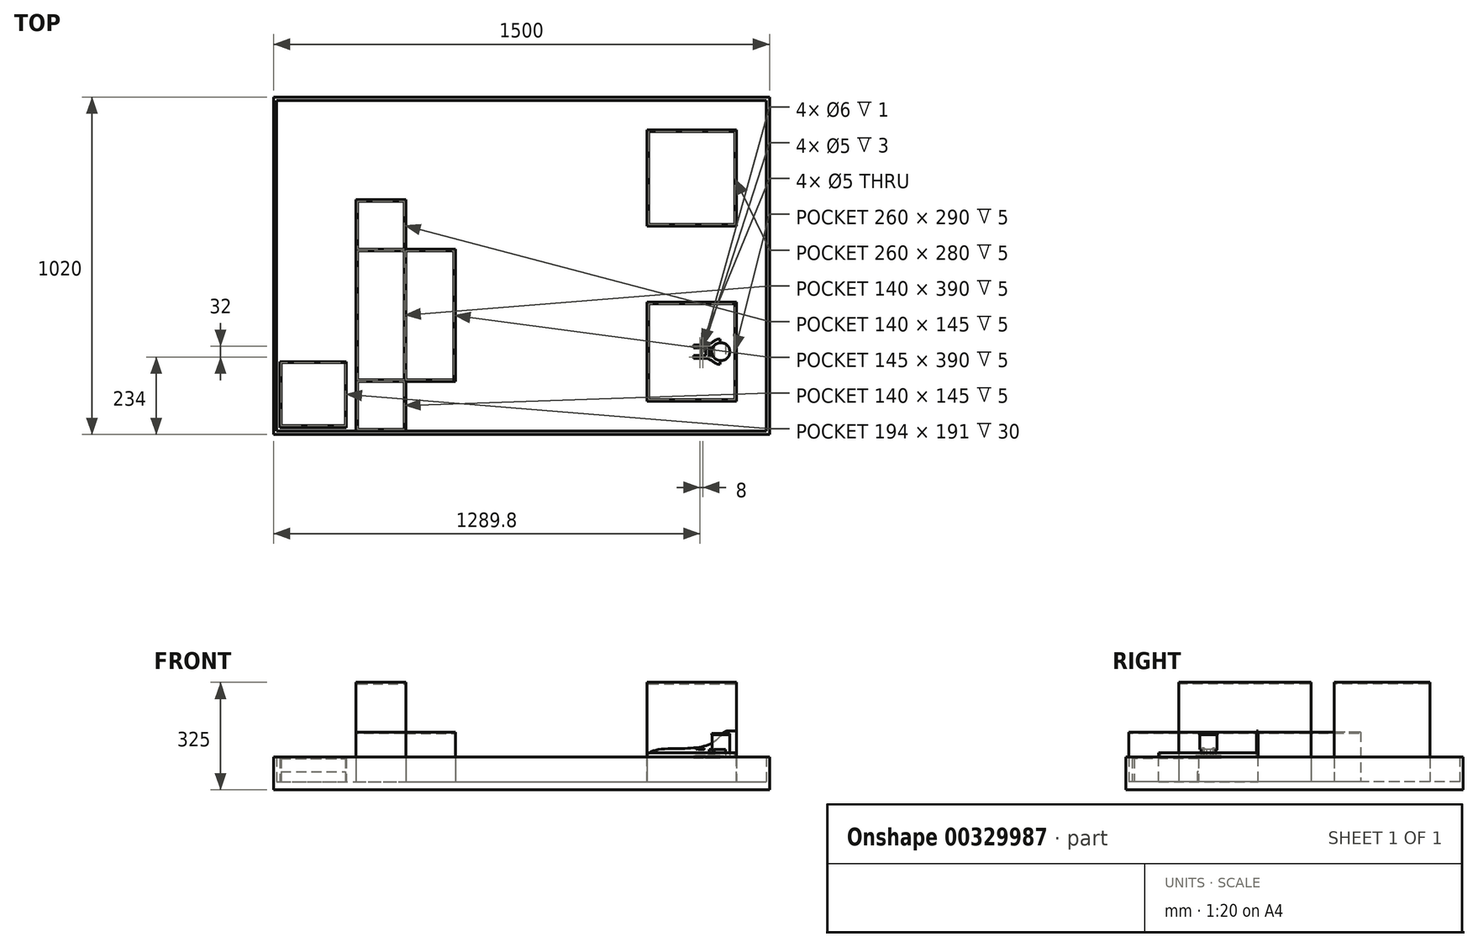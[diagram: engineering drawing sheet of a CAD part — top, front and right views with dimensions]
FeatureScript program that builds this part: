
annotation { "Feature Type Name" : "Feature", "Feature Type Description" : "" }
export const myFeature = defineFeature(function(context is Context, id is Id, definition is map)
    precondition{}
    {
        {
            var Q0;
            Q0=qCreatedBy(makeId("Top.planeOp"),FACE);
            var sketch = newSketch(context, id + "F0", { "sketchPlane" : qUnion([Q0])});
            skCircle(sketch, "E0", {"center": v(0, 0) * mm, "radius": 27.2 * mm});
            skSolve(sketch);
        }
        {
            var Q0;
            Q0=qSketchRegion(id+"F0",true);
            extrude(context, id + "F1", {"entities" : qUnion([Q0]), "depth" : 2.83 * mm});
        }
        {
            var Q0;
            Q0=makeQuery(id+"F1.opExtrude","CAP_FACE",FACE,{"disambiguationData":[OSD([sQuery(id+"F0.wireOp",EDGE,"E0")])],"isStart":false});
            var sketch = newSketch(context, id + "F2", { "sketchPlane" : qUnion([Q0])});
            skCircle(sketch, "E1", {"center": v(0, 0) * mm, "radius": 26.4 * mm});
            skSolve(sketch);
        }
        {
            var Q0;
            Q0=qSketchRegion(id+"F2",true);
            extrude(context, id + "F3", {"entities" : qUnion([Q0]), "operationType" : NewBodyOperationType.ADD, "depth" : 67.36 * mm});
        }
        {
            var Q0;
            Q0=makeQuery(id+"F3.opExtrude","CAP_FACE",FACE,{"disambiguationData":[OSD([sQuery(id+"F2.wireOp",EDGE,"E1")])],"isStart":false});
            var sketch = newSketch(context, id + "F4", { "sketchPlane" : qUnion([Q0])});
            skCircle(sketch, "E2", {"center": v(0, 0) * mm, "radius": 27.2 * mm});
            skSolve(sketch);
        }
        {
            var Q0;
            Q0=qSketchRegion(id+"F4",true);
            extrude(context, id + "F5", {"entities" : qUnion([Q0]), "operationType" : NewBodyOperationType.ADD, "depth" : 2.83 * mm});
        }
        {
            var Q0;
            Q0=makeQuery(id+"F5.opExtrude","CAP_FACE",FACE,{"disambiguationData":[OSD([sQuery(id+"F4.wireOp",EDGE,"E2")])],"isStart":false});
            var sketch = newSketch(context, id + "F6", { "sketchPlane" : qUnion([Q0])});
            skSolve(sketch);
        }
        {
            var Q0;
            Q0=qCreatedBy(makeId("Top.planeOp"),FACE);
            cPlane(context, id + "F7", {"entities" : qUnion([Q0]), "cplaneType" : CPlaneType.OFFSET, "offset" : 25 * mm, "width" : 150 * mm, "height" : 150 * mm});
        }
        {
            var Q0;
            Q0=makeQuery(id+"F6.imprint","IMPRINT",FACE,{"disambiguationData":[TD([[makeQuery(id+"F6.imprint","IMPRINT",EDGE,{"derivedFrom":makeQuery(id+"F5.opExtrude","CAP_EDGE",EDGE,{"disambiguationData":[OSD([sQuery(id+"F4.wireOp",EDGE,"E2")])],"isStart":false})}),1.0]])]});
            var sketch = newSketch(context, id + "F8", { "sketchPlane" : qUnion([Q0])});
            skSolve(sketch);
        }
        {
            var Q0;
            Q0=qCreatedBy(makeId("Top.planeOp"),FACE);
            var sketch = newSketch(context, id + "F9", { "sketchPlane" : qUnion([Q0])});
            skLineSegment(sketch, "E3.bottom", {"start": v(-222.8, -150) * mm, "end": v(47.2, -150) * mm});
            skLineSegment(sketch, "E3.top", {"start": v(-222.8, 150) * mm, "end": v(47.2, 150) * mm});
            skLineSegment(sketch, "E3.left", {"start": v(-222.8, -150) * mm, "end": v(-222.8, 150) * mm});
            skLineSegment(sketch, "E3.right", {"start": v(47.2, -150) * mm, "end": v(47.2, 150) * mm});
            skSolve(sketch);
        }
        {
            var Q0;
            Q0=qSketchRegion(id+"F9",true);
            extrude(context, id + "F10", {"entities" : qUnion([Q0]), "oppositeDirection" : true, "depth" : 72 * mm});
        }
        {
            var Q0;
            Q0=makeQuery(id+"F10.opExtrude","CAP_FACE",FACE,{"disambiguationData":[OSD([sQuery(id+"F9.wireOp",EDGE,"E3.bottom"),sQuery(id+"F9.wireOp",EDGE,"E3.top"),sQuery(id+"F9.wireOp",EDGE,"E3.left"),sQuery(id+"F9.wireOp",EDGE,"E3.right")])],"isStart":true});
            var sketch = newSketch(context, id + "F11", { "sketchPlane" : qUnion([Q0])});
            skLineSegment(sketch, "E4.bottom", {"start": v(-222.8, -150) * mm, "end": v(47.2, -150) * mm});
            skLineSegment(sketch, "E4.top", {"start": v(-222.8, -145) * mm, "end": v(42.2, -145) * mm});
            skLineSegment(sketch, "E4.left", {"start": v(-222.8, -150) * mm, "end": v(-222.8, -145) * mm});
            skLineSegment(sketch, "E5.bottom", {"start": v(47.2, 150) * mm, "end": v(42.2, 150) * mm});
            skLineSegment(sketch, "E5.left", {"start": v(47.2, 150) * mm, "end": v(47.2, -150) * mm});
            skLineSegment(sketch, "E5.right", {"start": v(42.2, 150) * mm, "end": v(42.2, -145) * mm});
            skSolve(sketch);
        }
        {
            var Q0;
            Q0=qSketchRegion(id+"F11",true);
            extrude(context, id + "F12", {"entities" : qUnion([Q0]), "operationType" : NewBodyOperationType.ADD, "depth" : 15 * mm});
        }
        {
            var Q0;
            Q0=makeQuery(id+"F12.boolean.opBoolean","MERGE",FACE,{"derivedFrom":[makeQuery(id+"F10.opExtrude","SWEPT_FACE",FACE,{"disambiguationData":[OSD([sQuery(id+"F9.wireOp",EDGE,"E3.top")])]}),makeQuery(id+"F12.opExtrude","SWEPT_FACE",FACE,{"disambiguationData":[OSD([sQuery(id+"F11.wireOp",EDGE,"E5.bottom")])]})]});
            var sketch = newSketch(context, id + "F13", { "sketchPlane" : qUnion([Q0])});
            skLineSegment(sketch, "E6", {"start": v(-47.2, 81.36) * mm, "end": v(-21.31, 81.36) * mm});
            skFitSpline(sketch, "E7", {"points": [v(-21.31, 81.36) * mm, v(15.24, 52.01) * mm, v(114.14, 28.17) * mm, v(222.8, 0) * mm], "startDerivative": vector(181.02, 0.3) * mm, "endDerivative": vector(-1.73, -239.85) * mm});
            skLineSegment(sketch, "E8", {"start": v(-47.2, 81.36) * mm, "end": v(-47.2, -72) * mm});
            skLineSegment(sketch, "E9", {"start": v(-47.2, -72) * mm, "end": v(222.8, -72) * mm});
            skLineSegment(sketch, "E10", {"start": v(222.8, -72) * mm, "end": v(222.8, 0) * mm});
            skSolve(sketch);
        }
        {
            var Q0;
            Q0=qSketchRegion(id+"F13",true);
            extrude(context, id + "F14", {"entities" : qUnion([Q0]), "operationType" : NewBodyOperationType.ADD, "oppositeDirection" : true, "depth" : 5 * mm});
        }
        {
            var Q0;
            Q0=makeQuery(id+"F10.opExtrude","CAP_FACE",FACE,{"disambiguationData":[OSD([sQuery(id+"F9.wireOp",EDGE,"E3.bottom"),sQuery(id+"F9.wireOp",EDGE,"E3.top"),sQuery(id+"F9.wireOp",EDGE,"E3.left"),sQuery(id+"F9.wireOp",EDGE,"E3.right")])],"isStart":true});
            var sketch = newSketch(context, id + "F15", { "sketchPlane" : qUnion([Q0])});
            skLineSegment(sketch, "E11.bottom", {"start": v(-222.8, 145) * mm, "end": v(-217.8, 145) * mm});
            skLineSegment(sketch, "E11.top", {"start": v(-222.8, -145) * mm, "end": v(-217.8, -145) * mm});
            skLineSegment(sketch, "E11.left", {"start": v(-222.8, 145) * mm, "end": v(-222.8, -145) * mm});
            skLineSegment(sketch, "E11.right", {"start": v(-217.8, 145) * mm, "end": v(-217.8, -145) * mm});
            skSolve(sketch);
        }
        {
            var Q0;
            Q0=qSketchRegion(id+"F15",true);
            extrude(context, id + "F16", {"entities" : qUnion([Q0]), "operationType" : NewBodyOperationType.ADD, "depth" : 5 * mm});
        }
        {
            var Q0;
            Q0=makeQuery(id+"F10.opExtrude","CAP_FACE",FACE,{"disambiguationData":[OSD([sQuery(id+"F9.wireOp",EDGE,"E3.bottom"),sQuery(id+"F9.wireOp",EDGE,"E3.top"),sQuery(id+"F9.wireOp",EDGE,"E3.left"),sQuery(id+"F9.wireOp",EDGE,"E3.right")])],"isStart":false});
            var sketch = newSketch(context, id + "F17", { "sketchPlane" : qUnion([Q0])});
            skLineSegment(sketch, "E12.bottom", {"start": v(147.2, 250) * mm, "end": v(-1352.8, 250) * mm});
            skLineSegment(sketch, "E12.top", {"start": v(147.2, -770) * mm, "end": v(-1352.8, -770) * mm});
            skLineSegment(sketch, "E12.left", {"start": v(147.2, 250) * mm, "end": v(147.2, -770) * mm});
            skLineSegment(sketch, "E12.right", {"start": v(-1352.8, 250) * mm, "end": v(-1352.8, -770) * mm});
            skSolve(sketch);
        }
        {
            var Q0;
            Q0=qSketchRegion(id+"F17",true);
            extrude(context, id + "F18", {"entities" : qUnion([Q0]), "operationType" : NewBodyOperationType.ADD, "depth" : 25 * mm});
        }
        {
            var Q0;
            Q0=makeQuery(id+"F18.opExtrude","CAP_FACE",FACE,{"disambiguationData":[OSD([sQuery(id+"F17.wireOp",EDGE,"E12.bottom"),sQuery(id+"F17.wireOp",EDGE,"E12.top"),sQuery(id+"F17.wireOp",EDGE,"E12.left"),sQuery(id+"F17.wireOp",EDGE,"E12.right")])],"isStart":true});
            var sketch = newSketch(context, id + "F19", { "sketchPlane" : qUnion([Q0])});
            skLineSegment(sketch, "E13.bottom", {"start": v(-222.8, 670) * mm, "end": v(47.2, 670) * mm});
            skLineSegment(sketch, "E13.top", {"start": v(-222.8, 380) * mm, "end": v(47.2, 380) * mm});
            skLineSegment(sketch, "E13.left", {"start": v(-222.8, 670) * mm, "end": v(-222.8, 380) * mm});
            skLineSegment(sketch, "E13.right", {"start": v(47.2, 670) * mm, "end": v(47.2, 380) * mm});
            skSolve(sketch);
        }
        {
            var Q0;
            Q0=qSketchRegion(id+"F19",true);
            extrude(context, id + "F20", {"entities" : qUnion([Q0]), "operationType" : NewBodyOperationType.ADD, "depth" : 300 * mm});
        }
        {
            var Q0;
            Q0=makeQuery(id+"F20.opExtrude","CAP_FACE",FACE,{"disambiguationData":[OSD([sQuery(id+"F19.wireOp",EDGE,"E13.bottom"),sQuery(id+"F19.wireOp",EDGE,"E13.top"),sQuery(id+"F19.wireOp",EDGE,"E13.left"),sQuery(id+"F19.wireOp",EDGE,"E13.right")])],"isStart":false});
            var sketch = newSketch(context, id + "F21", { "sketchPlane" : qUnion([Q0])});
            skLineSegment(sketch, "E14.bottom", {"start": v(-217.8, 665) * mm, "end": v(42.2, 665) * mm});
            skLineSegment(sketch, "E14.top", {"start": v(-217.8, 385) * mm, "end": v(42.2, 385) * mm});
            skLineSegment(sketch, "E14.left", {"start": v(-217.8, 665) * mm, "end": v(-217.8, 385) * mm});
            skLineSegment(sketch, "E14.right", {"start": v(42.2, 665) * mm, "end": v(42.2, 385) * mm});
            skSolve(sketch);
        }
        {
            var Q0;
            Q0=qSketchRegion(id+"F21",true);
            extrude(context, id + "F22", {"entities" : qUnion([Q0]), "operationType" : NewBodyOperationType.REMOVE, "oppositeDirection" : true, "depth" : 5 * mm});
        }
        {
            var Q0;
            Q0=makeQuery(id+"F18.opExtrude","CAP_FACE",FACE,{"disambiguationData":[OSD([sQuery(id+"F17.wireOp",EDGE,"E12.bottom"),sQuery(id+"F17.wireOp",EDGE,"E12.top"),sQuery(id+"F17.wireOp",EDGE,"E12.left"),sQuery(id+"F17.wireOp",EDGE,"E12.right")])],"isStart":true});
            var sketch = newSketch(context, id + "F23", { "sketchPlane" : qUnion([Q0])});
            skLineSegment(sketch, "E15.bottom", {"start": v(-1352.8, 770) * mm, "end": v(147.2, 770) * mm});
            skLineSegment(sketch, "E15.top", {"start": v(-1352.8, -250) * mm, "end": v(147.2, -250) * mm});
            skLineSegment(sketch, "E15.left", {"start": v(-1352.8, 770) * mm, "end": v(-1352.8, -250) * mm});
            skLineSegment(sketch, "E15.right", {"start": v(147.2, 770) * mm, "end": v(147.2, -250) * mm});
            skLineSegment(sketch, "E16.bottom", {"start": v(-1342.8, 760) * mm, "end": v(137.2, 760) * mm});
            skLineSegment(sketch, "E16.top", {"start": v(-1342.8, -240) * mm, "end": v(137.2, -240) * mm});
            skLineSegment(sketch, "E16.left", {"start": v(-1342.8, 760) * mm, "end": v(-1342.8, -240) * mm});
            skLineSegment(sketch, "E16.right", {"start": v(137.2, 760) * mm, "end": v(137.2, -240) * mm});
            skSolve(sketch);
        }
        {
            var Q0;
            Q0=qSketchRegion(id+"F23",true);
            extrude(context, id + "F24", {"entities" : qUnion([Q0]), "operationType" : NewBodyOperationType.ADD, "depth" : 75 * mm});
        }
        {
            var Q0;
            Q0=makeQuery(id+"F18.opExtrude","CAP_FACE",FACE,{"disambiguationData":[OSD([sQuery(id+"F17.wireOp",EDGE,"E12.bottom"),sQuery(id+"F17.wireOp",EDGE,"E12.top"),sQuery(id+"F17.wireOp",EDGE,"E12.left"),sQuery(id+"F17.wireOp",EDGE,"E12.right")])],"isStart":true});
            var sketch = newSketch(context, id + "F25", { "sketchPlane" : qUnion([Q0])});
            skLineSegment(sketch, "E17.bottom", {"start": v(-1102.8, 460) * mm, "end": v(-952.8, 460) * mm});
            skLineSegment(sketch, "E17.top", {"start": v(-1102.8, -240) * mm, "end": v(-952.8, -240) * mm});
            skLineSegment(sketch, "E17.left", {"start": v(-1102.8, 460) * mm, "end": v(-1102.8, -240) * mm});
            skLineSegment(sketch, "E17.right", {"start": v(-952.8, 460) * mm, "end": v(-952.8, 310) * mm});
            skLineSegment(sketch, "E18.bottom", {"start": v(-952.8, 310) * mm, "end": v(-802.8, 310) * mm});
            skLineSegment(sketch, "E18.top", {"start": v(-952.8, -90) * mm, "end": v(-802.8, -90) * mm});
            skLineSegment(sketch, "E18.right", {"start": v(-802.8, 310) * mm, "end": v(-802.8, -90) * mm});
            skLineSegment(sketch, "E19.trimOffspring", {"start": v(-952.8, -90) * mm, "end": v(-952.8, -240) * mm});
            skSolve(sketch);
        }
        {
            var Q0;
            Q0=qSketchRegion(id+"F25",true);
            extrude(context, id + "F26", {"entities" : qUnion([Q0]), "operationType" : NewBodyOperationType.ADD, "depth" : 150 * mm});
        }
        {
            var Q0;
            Q0=makeQuery(id+"F26.opExtrude","CAP_FACE",FACE,{"disambiguationData":[OSD([sQuery(id+"F25.wireOp",EDGE,"E17.bottom"),sQuery(id+"F25.wireOp",EDGE,"E17.top"),sQuery(id+"F25.wireOp",EDGE,"E17.left"),sQuery(id+"F25.wireOp",EDGE,"E17.right"),sQuery(id+"F25.wireOp",EDGE,"E18.bottom"),sQuery(id+"F25.wireOp",EDGE,"E18.top"),sQuery(id+"F25.wireOp",EDGE,"E18.right"),sQuery(id+"F25.wireOp",EDGE,"E19.trimOffspring")])],"isStart":false});
            var sketch = newSketch(context, id + "F27", { "sketchPlane" : qUnion([Q0])});
            skLineSegment(sketch, "E20.bottom", {"start": v(-952.8, 310) * mm, "end": v(-1102.8, 310) * mm});
            skLineSegment(sketch, "E20.top", {"start": v(-952.8, -90) * mm, "end": v(-1102.8, -90) * mm});
            skLineSegment(sketch, "E20.left", {"start": v(-952.8, 310) * mm, "end": v(-952.8, -90) * mm});
            skLineSegment(sketch, "E20.right", {"start": v(-1102.8, 310) * mm, "end": v(-1102.8, -90) * mm});
            skSolve(sketch);
        }
        {
            var Q0;
            Q0=qSketchRegion(id+"F27",true);
            extrude(context, id + "F28", {"entities" : qUnion([Q0]), "operationType" : NewBodyOperationType.ADD, "depth" : 150 * mm});
        }
        {
            var Q0;
            Q0=makeQuery(id+"F28.opExtrude","CAP_FACE",FACE,{"disambiguationData":[OSD([sQuery(id+"F27.wireOp",EDGE,"E20.bottom"),sQuery(id+"F27.wireOp",EDGE,"E20.top"),sQuery(id+"F27.wireOp",EDGE,"E20.left"),sQuery(id+"F27.wireOp",EDGE,"E20.right")])],"isStart":false});
            var sketch = newSketch(context, id + "F29", { "sketchPlane" : qUnion([Q0])});
            skLineSegment(sketch, "E21.bottom", {"start": v(-1097.8, 305) * mm, "end": v(-957.8, 305) * mm});
            skLineSegment(sketch, "E21.top", {"start": v(-1097.8, -85) * mm, "end": v(-957.8, -85) * mm});
            skLineSegment(sketch, "E21.left", {"start": v(-1097.8, 305) * mm, "end": v(-1097.8, -85) * mm});
            skLineSegment(sketch, "E21.right", {"start": v(-957.8, 305) * mm, "end": v(-957.8, -85) * mm});
            skSolve(sketch);
        }
        {
            var Q0;
            Q0=qSketchRegion(id+"F29",true);
            extrude(context, id + "F30", {"entities" : qUnion([Q0]), "operationType" : NewBodyOperationType.REMOVE, "oppositeDirection" : true, "depth" : 5 * mm});
        }
        {
            var Q0;
            {var subQ0=sQuery(id+"F25.wireOp",EDGE,"E17.left");var subQ1=sQuery(id+"F25.wireOp",EDGE,"E18.bottom");var subQ2=sQuery(id+"F25.wireOp",EDGE,"E17.right");var subQ3=sQuery(id+"F25.wireOp",EDGE,"E17.bottom");var subQ4=makeQuery(id+"F26.opExtrude","CAP_FACE",FACE,{"disambiguationData":[OSD([subQ3,sQuery(id+"F25.wireOp",EDGE,"E17.top"),subQ0,subQ2,subQ1,sQuery(id+"F25.wireOp",EDGE,"E18.top"),sQuery(id+"F25.wireOp",EDGE,"E18.right"),sQuery(id+"F25.wireOp",EDGE,"E19.trimOffspring")])],"isStart":false});Q0=makeQuery(id+"F28.boolean.opBoolean","SPLIT",FACE,{"disambiguationData":[TD([makeQuery(id+"F26.opExtrude","SWEPT_FACE",FACE,{"disambiguationData":[OSD([subQ3])]})])],"derivedFrom":subQ4});}
            var sketch = newSketch(context, id + "F31", { "sketchPlane" : qUnion([Q0])});
            skLineSegment(sketch, "E22.bottom", {"start": v(-1097.8, 455) * mm, "end": v(-957.8, 455) * mm});
            skLineSegment(sketch, "E22.top", {"start": v(-1097.8, 310) * mm, "end": v(-957.8, 310) * mm});
            skLineSegment(sketch, "E22.left", {"start": v(-1097.8, 455) * mm, "end": v(-1097.8, 310) * mm});
            skLineSegment(sketch, "E22.right", {"start": v(-957.8, 455) * mm, "end": v(-957.8, 310) * mm});
            skLineSegment(sketch, "E23.bottom", {"start": v(-952.8, 305) * mm, "end": v(-807.8, 305) * mm});
            skLineSegment(sketch, "E23.top", {"start": v(-952.8, -85) * mm, "end": v(-807.8, -85) * mm});
            skLineSegment(sketch, "E23.left", {"start": v(-952.8, 305) * mm, "end": v(-952.8, -85) * mm});
            skLineSegment(sketch, "E23.right", {"start": v(-807.8, 305) * mm, "end": v(-807.8, -85) * mm});
            skLineSegment(sketch, "E24.bottom", {"start": v(-1097.8, -90) * mm, "end": v(-957.8, -90) * mm});
            skLineSegment(sketch, "E24.top", {"start": v(-1097.8, -235) * mm, "end": v(-957.8, -235) * mm});
            skLineSegment(sketch, "E24.left", {"start": v(-1097.8, -90) * mm, "end": v(-1097.8, -235) * mm});
            skLineSegment(sketch, "E24.right", {"start": v(-957.8, -90) * mm, "end": v(-957.8, -235) * mm});
            skSolve(sketch);
        }
        {
            var Q0;
            Q0=qSketchRegion(id+"F31",true);
            extrude(context, id + "F32", {"entities" : qUnion([Q0]), "operationType" : NewBodyOperationType.REMOVE, "oppositeDirection" : true, "depth" : 5 * mm});
        }
        {
            var Q0;
            Q0=qCreatedBy(id+"F7.planeOp",FACE);
            var sketch = newSketch(context, id + "F33", { "sketchPlane" : qUnion([Q0])});
            skLineSegment(sketch, "E25", {"start": v(0, 0) * mm, "end": v(-90, 0) * mm, "construction": true});
            skLineSegment(sketch, "E26.bottom", {"start": v(-74.5, -12) * mm, "end": v(-55, -12) * mm});
            skLineSegment(sketch, "E26.top", {"start": v(-74.5, -20) * mm, "end": v(-55, -20) * mm});
            skLineSegment(sketch, "E26.left", {"start": v(-74.5, -12) * mm, "end": v(-74.5, -13) * mm});
            skPoint(sketch, "E27.visualSharp", {"position": v(-51, -12) * mm});
            skPoint(sketch, "E28.visualSharp", {"position": v(-51, -20) * mm});
            skCircle(sketch, "E29", {"center": v(-55, -16) * mm, "radius": 3 * mm});
            skLineSegment(sketch, "E30", {"start": v(-59, -3.98) * mm, "end": v(-59, -18.08) * mm, "construction": true});
            skCircle(sketch, "E31.MirrorC", {"center": v(-63, -16) * mm, "radius": 3 * mm});
            skLineSegment(sketch, "E32.bottom", {"start": v(-74.5, -13) * mm, "end": v(-65.65, -13) * mm});
            skLineSegment(sketch, "E32.top", {"start": v(-74.5, -19) * mm, "end": v(-65.65, -19) * mm});
            skArc(sketch, "E33", {"start": v(-65.65, -13) * mm, "mid": v(-67, -16) * mm, "end": v(-65.65, -19) * mm});
            skLineSegment(sketch, "E34.trimOffspring", {"start": v(-74.5, -19) * mm, "end": v(-74.5, -20) * mm});
            skArc(sketch, "E35.trimOffspring", {"start": v(-55, -20) * mm, "mid": v(-51, -16) * mm, "end": v(-55, -12) * mm});
            skLineSegment(sketch, "E36.MirrorCS", {"start": v(-74.5, 12) * mm, "end": v(-74.5, 13) * mm});
            skLineSegment(sketch, "E37.MirrorCS", {"start": v(-74.5, 19) * mm, "end": v(-74.5, 20) * mm});
            skPoint(sketch, "E38.MirrorP", {"position": v(-51, 12) * mm});
            skLineSegment(sketch, "E39.MirrorCS", {"start": v(-74.5, 12) * mm, "end": v(-55, 12) * mm});
            skPoint(sketch, "E40.MirrorP", {"position": v(-51, 20) * mm});
            skArc(sketch, "E41.MirrorCS", {"start": v(-65.65, 13) * mm, "mid": v(-67, 16) * mm, "end": v(-65.65, 19) * mm});
            skArc(sketch, "E42.MirrorCS", {"start": v(-55, 20) * mm, "mid": v(-51, 16) * mm, "end": v(-55, 12) * mm});
            skLineSegment(sketch, "E43.MirrorCS", {"start": v(-74.5, 20) * mm, "end": v(-55, 20) * mm});
            skCircle(sketch, "E44.MirrorC", {"center": v(-55, 16) * mm, "radius": 3 * mm});
            skCircle(sketch, "E45.MirrorC", {"center": v(-63, 16) * mm, "radius": 3 * mm});
            skLineSegment(sketch, "E46.MirrorCS", {"start": v(-74.5, 19) * mm, "end": v(-65.65, 19) * mm});
            skLineSegment(sketch, "E47.MirrorCS", {"start": v(-74.5, 13) * mm, "end": v(-65.65, 13) * mm});
            skSolve(sketch);
        }
        {
            var Q0;
            Q0=qSketchRegion(id+"F33",true);
            var Q1;
            Q1=qSketchRegion(id+"F36",true);
            extrude(context, id + "F34", {"entities" : qUnion([Q0, Q1]), "endBound" : BoundingType.SYMMETRIC, "depth" : 8 * mm});
        }
        {
            var Q0;
            Q0=makeQuery(id+"F34.opExtrude","CAP_EDGE",EDGE,{"disambiguationData":[OSD([sQuery(id+"F33.wireOp",EDGE,"E34.trimOffspring")])],"isStart":false});
            var Q1;
            Q1=makeQuery(id+"F34.opExtrude","CAP_EDGE",EDGE,{"disambiguationData":[OSD([sQuery(id+"F33.wireOp",EDGE,"E26.left")])],"isStart":false});
            var Q2;
            Q2=makeQuery(id+"F34.opExtrude","CAP_EDGE",EDGE,{"disambiguationData":[OSD([sQuery(id+"F33.wireOp",EDGE,"E34.trimOffspring")])],"isStart":true});
            var Q3;
            Q3=makeQuery(id+"F34.opExtrude","CAP_EDGE",EDGE,{"disambiguationData":[OSD([sQuery(id+"F33.wireOp",EDGE,"E26.left")])],"isStart":true});
            var Q4;
            Q4=makeQuery(id+"F34.opExtrude","CAP_EDGE",EDGE,{"disambiguationData":[OSD([sQuery(id+"F33.wireOp",EDGE,"E36.MirrorCS")])],"isStart":false});
            var Q5;
            Q5=makeQuery(id+"F34.opExtrude","CAP_EDGE",EDGE,{"disambiguationData":[OSD([sQuery(id+"F33.wireOp",EDGE,"E37.MirrorCS")])],"isStart":false});
            var Q6;
            Q6=makeQuery(id+"F34.opExtrude","CAP_EDGE",EDGE,{"disambiguationData":[OSD([sQuery(id+"F33.wireOp",EDGE,"E37.MirrorCS")])],"isStart":true});
            var Q7;
            Q7=makeQuery(id+"F34.opExtrude","CAP_EDGE",EDGE,{"disambiguationData":[OSD([sQuery(id+"F33.wireOp",EDGE,"E36.MirrorCS")])],"isStart":true});
            fillet(context, id + "F35", {"entities" : qUnion([Q0, Q1, Q2, Q3, Q4, Q5, Q6, Q7]), "radius" : 4 * mm, "tangentPropagation" : true, "allowEdgeOverflow" : false});
        }
        {
            var Q0;
            Q0=makeQuery(id+"F34.opExtrude","SWEPT_FACE",FACE,{"disambiguationData":[OSD([sQuery(id+"F33.wireOp",EDGE,"E26.top")])]});
            var sketch = newSketch(context, id + "F36", { "sketchPlane" : qUnion([Q0])});
            skCircle(sketch, "E48", {"center": v(-70.5, 25) * mm, "radius": 3 * mm});
            skSolve(sketch);
        }
        {
            var Q0;
            Q0=qSketchRegion(id+"F36",true);
            var Q1;
            Q1=makeQuery(id+"F34.opExtrude","SWEPT_FACE",FACE,{"disambiguationData":[OSD([sQuery(id+"F33.wireOp",EDGE,"E26.bottom")])]});
            extrude(context, id + "F37", {"entities" : qUnion([Q0]), "operationType" : NewBodyOperationType.ADD, "endBound" : BoundingType.UP_TO_SURFACE, "oppositeDirection" : true, "endBoundEntityFace" : qUnion([Q1]), "depth" : 25 * mm});
        }
        {
            var Q0;
            Q0=makeQuery(id+"F34.opExtrude","SWEPT_FACE",FACE,{"disambiguationData":[OSD([sQuery(id+"F33.wireOp",EDGE,"E43.MirrorCS")])]});
            var sketch = newSketch(context, id + "F38", { "sketchPlane" : qUnion([Q0])});
            skCircle(sketch, "E49", {"center": v(70.5, 25) * mm, "radius": 3 * mm});
            skSolve(sketch);
        }
        {
            var Q0;
            Q0=qSketchRegion(id+"F38",true);
            var Q1;
            Q1=makeQuery(id+"F34.opExtrude","SWEPT_FACE",FACE,{"disambiguationData":[OSD([sQuery(id+"F33.wireOp",EDGE,"E39.MirrorCS")])]});
            extrude(context, id + "F39", {"entities" : qUnion([Q0]), "operationType" : NewBodyOperationType.ADD, "endBound" : BoundingType.UP_TO_SURFACE, "oppositeDirection" : true, "endBoundEntityFace" : qUnion([Q1]), "depth" : 25 * mm});
        }
        {
            var Q0;
            Q0=qCreatedBy(id+"F7.planeOp",FACE);
            var sketch = newSketch(context, id + "F40", { "sketchPlane" : qUnion([Q0])});
            skCircle(sketch, "E50", {"center": v(-55, 16) * mm, "radius": 3 * mm});
            skCircle(sketch, "E51", {"center": v(-63, 16) * mm, "radius": 2.5 * mm});
            skCircle(sketch, "E52", {"center": v(-63, 16) * mm, "radius": 3 * mm});
            skCircle(sketch, "E53", {"center": v(-55, 16) * mm, "radius": 2.5 * mm});
            skSolve(sketch);
        }
        {
            var Q0;
            Q0=qSketchRegion(id+"F40",true);
            extrude(context, id + "F41", {"entities" : qUnion([Q0]), "operationType" : NewBodyOperationType.ADD, "endBound" : BoundingType.SYMMETRIC, "depth" : 6 * mm});
        }
        {
            var Q0;
            Q0=qCreatedBy(id+"F7.planeOp",FACE);
            var sketch = newSketch(context, id + "F42", { "sketchPlane" : qUnion([Q0])});
            skCircle(sketch, "E54", {"center": v(-63, -16) * mm, "radius": 2.5 * mm});
            skCircle(sketch, "E55", {"center": v(-63, -16) * mm, "radius": 3 * mm});
            skCircle(sketch, "E56", {"center": v(-55, -16) * mm, "radius": 2.5 * mm});
            skCircle(sketch, "E57", {"center": v(-55, -16) * mm, "radius": 3 * mm});
            skSolve(sketch);
        }
        {
            var Q0;
            Q0=qSketchRegion(id+"F42",true);
            extrude(context, id + "F43", {"entities" : qUnion([Q0]), "operationType" : NewBodyOperationType.ADD, "endBound" : BoundingType.SYMMETRIC, "depth" : 6 * mm});
        }
        {
            var Q0;
            Q0=makeQuery(id+"F34.opExtrude","SWEPT_FACE",FACE,{"disambiguationData":[OSD([sQuery(id+"F33.wireOp",EDGE,"E43.MirrorCS")])]});
            var sketch = newSketch(context, id + "F44", { "sketchPlane" : qUnion([Q0])});
            skArc(sketch, "E58", {"start": v(71.5, 27.3) * mm, "mid": v(70.5, 27.5) * mm, "end": v(69.5, 27.3) * mm});
            skLineSegment(sketch, "E59.bottom", {"start": v(68.2, 26) * mm, "end": v(69.5, 26) * mm});
            skLineSegment(sketch, "E59.top", {"start": v(68.2, 24) * mm, "end": v(69.5, 24) * mm});
            skLineSegment(sketch, "E60.left", {"start": v(71.5, 27.3) * mm, "end": v(71.5, 26) * mm});
            skLineSegment(sketch, "E60.right", {"start": v(69.5, 27.3) * mm, "end": v(69.5, 26) * mm});
            skPoint(sketch, "E61.orphan", {"position": v(69.5, 27.8) * mm});
            skPoint(sketch, "E62.orphan", {"position": v(71.5, 27.8) * mm});
            skArc(sketch, "E63.trimOffspring", {"start": v(68.2, 26) * mm, "mid": v(68, 25) * mm, "end": v(68.2, 24) * mm});
            skPoint(sketch, "E59.left.start.orphan", {"position": v(67.32, 26) * mm});
            skPoint(sketch, "E64.orphan", {"position": v(67.32, 24) * mm});
            skArc(sketch, "E65.trimOffspring", {"start": v(69.5, 22.7) * mm, "mid": v(70.5, 22.5) * mm, "end": v(71.5, 22.7) * mm});
            skLineSegment(sketch, "E66.trimOffspring", {"start": v(69.5, 24) * mm, "end": v(69.5, 22.7) * mm});
            skLineSegment(sketch, "E67.trimOffspring", {"start": v(71.5, 26) * mm, "end": v(72.8, 26) * mm});
            skLineSegment(sketch, "E68.trimOffspring", {"start": v(71.5, 24) * mm, "end": v(71.5, 22.7) * mm});
            skLineSegment(sketch, "E69.trimOffspring", {"start": v(71.5, 24) * mm, "end": v(72.8, 24) * mm});
            skPoint(sketch, "E60.top.end.orphan", {"position": v(69.5, 22.2) * mm});
            skPoint(sketch, "E70.orphan", {"position": v(71.5, 22.2) * mm});
            skPoint(sketch, "E59.right.end.orphan", {"position": v(73.68, 24) * mm});
            skPoint(sketch, "E71.orphan", {"position": v(73.68, 26) * mm});
            skArc(sketch, "E72.trimOffspring", {"start": v(72.8, 24) * mm, "mid": v(73, 25) * mm, "end": v(72.8, 26) * mm});
            skSolve(sketch);
        }
        {
            var Q0;
            Q0=qSketchRegion(id+"F44",true);
            extrude(context, id + "F45", {"entities" : qUnion([Q0]), "operationType" : NewBodyOperationType.REMOVE, "endBound" : BoundingType.THROUGH_ALL, "oppositeDirection" : true, "depth" : 25 * mm});
        }
        {
            var Q0;
            Q0=makeQuery(id+"F18.opExtrude","CAP_FACE",FACE,{"disambiguationData":[OSD([sQuery(id+"F17.wireOp",EDGE,"E12.bottom"),sQuery(id+"F17.wireOp",EDGE,"E12.top"),sQuery(id+"F17.wireOp",EDGE,"E12.left"),sQuery(id+"F17.wireOp",EDGE,"E12.right")])],"isStart":true});
            var sketch = newSketch(context, id + "F46", { "sketchPlane" : qUnion([Q0])});
            skLineSegment(sketch, "E73.bottom", {"start": v(-1332.8, -30) * mm, "end": v(-1132.8, -30) * mm});
            skLineSegment(sketch, "E73.top", {"start": v(-1332.8, -230) * mm, "end": v(-1132.8, -230) * mm});
            skLineSegment(sketch, "E73.left", {"start": v(-1332.8, -30) * mm, "end": v(-1332.8, -230) * mm});
            skLineSegment(sketch, "E73.right", {"start": v(-1132.8, -30) * mm, "end": v(-1132.8, -230) * mm});
            skLineSegment(sketch, "E74.bottom", {"start": v(-1329.8, -33) * mm, "end": v(-1135.8, -33) * mm});
            skLineSegment(sketch, "E74.top", {"start": v(-1329.8, -224) * mm, "end": v(-1135.8, -224) * mm});
            skLineSegment(sketch, "E74.left", {"start": v(-1329.8, -33) * mm, "end": v(-1329.8, -224) * mm});
            skLineSegment(sketch, "E74.right", {"start": v(-1135.8, -33) * mm, "end": v(-1135.8, -224) * mm});
            skSolve(sketch);
        }
        {
            var Q0;
            Q0=qSketchRegion(id+"F46",true);
            extrude(context, id + "F47", {"entities" : qUnion([Q0]), "operationType" : NewBodyOperationType.ADD, "depth" : 30 * mm});
        }
        {
            var Q0;
            Q0=makeQuery(id+"F47.opExtrude","CAP_FACE",FACE,{"disambiguationData":[OSD([sQuery(id+"F46.wireOp",EDGE,"E73.bottom"),sQuery(id+"F46.wireOp",EDGE,"E73.top"),sQuery(id+"F46.wireOp",EDGE,"E73.left"),sQuery(id+"F46.wireOp",EDGE,"E73.right"),sQuery(id+"F46.wireOp",EDGE,"E74.bottom"),sQuery(id+"F46.wireOp",EDGE,"E74.top"),sQuery(id+"F46.wireOp",EDGE,"E74.left"),sQuery(id+"F46.wireOp",EDGE,"E74.right")])],"isStart":false});
            var sketch = newSketch(context, id + "F48", { "sketchPlane" : qUnion([Q0])});
            skLineSegment(sketch, "E75.bottom", {"start": v(-1332.8, -30) * mm, "end": v(-1329.8, -30) * mm});
            skLineSegment(sketch, "E75.top", {"start": v(-1332.8, -230) * mm, "end": v(-1329.8, -230) * mm});
            skLineSegment(sketch, "E75.left", {"start": v(-1332.8, -30) * mm, "end": v(-1332.8, -230) * mm});
            skLineSegment(sketch, "E75.right", {"start": v(-1329.8, -30) * mm, "end": v(-1329.8, -224) * mm});
            skLineSegment(sketch, "E76.bottom", {"start": v(-1329.8, -230) * mm, "end": v(-1135.8, -230) * mm});
            skLineSegment(sketch, "E76.top", {"start": v(-1329.8, -224) * mm, "end": v(-1135.8, -224) * mm});
            skLineSegment(sketch, "E77.bottom", {"start": v(-1135.8, -230) * mm, "end": v(-1132.8, -230) * mm});
            skLineSegment(sketch, "E77.top", {"start": v(-1135.8, -30) * mm, "end": v(-1132.8, -30) * mm});
            skLineSegment(sketch, "E77.left", {"start": v(-1135.8, -224) * mm, "end": v(-1135.8, -30) * mm});
            skLineSegment(sketch, "E77.right", {"start": v(-1132.8, -230) * mm, "end": v(-1132.8, -30) * mm});
            skSolve(sketch);
        }
        {
            var Q0;
            Q0=qSketchRegion(id+"F48",true);
            extrude(context, id + "F49", {"entities" : qUnion([Q0]), "operationType" : NewBodyOperationType.ADD, "depth" : 40 * mm});
        }
        {
            var Q0;
            Q0=makeQuery(id+"F9.imprint","IMPRINT",FACE,{"disambiguationData":[TD([[makeQuery(id+"F9.imprint","IMPRINT",EDGE,{"derivedFrom":sQuery(id+"F9.wireOp",EDGE,"E3.bottom")}),1.0]])]});
            var sketch = newSketch(context, id + "F50", { "sketchPlane" : qUnion([Q0])});
            skLineSegment(sketch, "E78", {"start": v(-46.72, 20) * mm, "end": v(-82.85, 20) * mm});
            skLineSegment(sketch, "E79", {"start": v(-82.85, 20) * mm, "end": v(-82.85, 12) * mm});
            skLineSegment(sketch, "E80", {"start": v(-82.85, 12) * mm, "end": v(-45.56, 12) * mm});
            skLineSegment(sketch, "E81", {"start": v(-45.56, 12) * mm, "end": v(-45.56, -12) * mm});
            skLineSegment(sketch, "E82", {"start": v(-45.56, -12) * mm, "end": v(-82.85, -12) * mm});
            skLineSegment(sketch, "E83", {"start": v(-82.85, -12) * mm, "end": v(-82.85, -20) * mm});
            skLineSegment(sketch, "E84", {"start": v(-82.85, -20) * mm, "end": v(-45.56, -20) * mm});
            skLineSegment(sketch, "E85", {"start": v(-106.47, 0) * mm, "end": v(11.1, 0) * mm, "construction": true});
            skFitSpline(sketch, "E86", {"points": [v(-46.72, 20) * mm, v(-2.86, 38.5) * mm], "startDerivative": vector(47.58, -3.14) * mm, "endDerivative": vector(53.64, -1.25) * mm});
            skFitSpline(sketch, "E87.MirrorCS", {"points": [v(-46.72, -20) * mm, v(-2.86, -38.5) * mm], "startDerivative": vector(47.58, 3.14) * mm, "endDerivative": vector(53.64, 1.25) * mm});
            skArc(sketch, "E88", {"start": v(-2.86, 27.05) * mm, "mid": v(-18.28, 20.14) * mm, "end": v(-26.64, 5.47) * mm});
            skLineSegment(sketch, "E89", {"start": v(-2.86, 38.5) * mm, "end": v(-2.86, 27.05) * mm});
            skLineSegment(sketch, "E90.trimOffspring", {"start": v(-2.86, -27.05) * mm, "end": v(-2.86, -38.5) * mm});
            skLineSegment(sketch, "E91", {"start": v(-31.8, 0) * mm, "end": v(-31.8, 6) * mm});
            skLineSegment(sketch, "E92", {"start": v(-31.8, 6) * mm, "end": v(-26.82, 5.5) * mm});
            skLineSegment(sketch, "E93.MirrorCS", {"start": v(-31.8, 0) * mm, "end": v(-31.8, -6) * mm});
            skLineSegment(sketch, "E94.MirrorCS", {"start": v(-31.8, -6) * mm, "end": v(-26.82, -5.5) * mm});
            skLineSegment(sketch, "E95", {"start": v(-26.82, 5.5) * mm, "end": v(-26.64, 5.47) * mm});
            skLineSegment(sketch, "E96", {"start": v(-26.64, -5.47) * mm, "end": v(-26.82, -5.5) * mm});
            skPoint(sketch, "E97.end.orphan", {"position": v(-27.2, 0) * mm});
            skPoint(sketch, "E98.MirrorCS.start.orphan", {"position": v(-26.82, -5.5) * mm});
            skArc(sketch, "E99.trimOffspring", {"start": v(-26.64, -5.47) * mm, "mid": v(-18.28, -20.14) * mm, "end": v(-2.86, -27.05) * mm});
            skCircle(sketch, "E100", {"center": v(-63, -16) * mm, "radius": 2.5 * mm});
            skCircle(sketch, "E101", {"center": v(-55, -16) * mm, "radius": 2.5 * mm});
            skCircle(sketch, "E102.MirrorC", {"center": v(-63, 16) * mm, "radius": 2.5 * mm});
            skCircle(sketch, "E103.MirrorC", {"center": v(-55, 16) * mm, "radius": 2.5 * mm});
            skSolve(sketch);
        }
        {
            var Q0;
            Q0 = qSketchRegion(id + "F50", true);
            extrude(context, id + "F51", {"entities" : qUnion([Q0]), "depth" : 25 * mm});
        }
        {
            var Q0;
            Q0=makeQuery(id+"F51.opExtrude","CAP_FACE",FACE,{"disambiguationData":[OSD([sQuery(id+"F50.wireOp",EDGE,"E78"),sQuery(id+"F50.wireOp",EDGE,"E79"),sQuery(id+"F50.wireOp",EDGE,"E80"),sQuery(id+"F50.wireOp",EDGE,"E81"),sQuery(id+"F50.wireOp",EDGE,"E82"),sQuery(id+"F50.wireOp",EDGE,"E83"),sQuery(id+"F50.wireOp",EDGE,"E84"),sQuery(id+"F50.wireOp",EDGE,"E86"),sQuery(id+"F50.wireOp",EDGE,"E87.MirrorCS"),sQuery(id+"F50.wireOp",EDGE,"E88"),sQuery(id+"F50.wireOp",EDGE,"E89"),sQuery(id+"F50.wireOp",EDGE,"E90.trimOffspring"),sQuery(id+"F50.wireOp",EDGE,"E91"),sQuery(id+"F50.wireOp",EDGE,"E92"),sQuery(id+"F50.wireOp",EDGE,"E93.MirrorCS"),sQuery(id+"F50.wireOp",EDGE,"E94.MirrorCS"),sQuery(id+"F50.wireOp",EDGE,"E95"),sQuery(id+"F50.wireOp",EDGE,"E96"),sQuery(id+"F50.wireOp",EDGE,"E99.trimOffspring")])],"isStart":false});
            var sketch = newSketch(context, id + "F52", { "sketchPlane" : qUnion([Q0])});
            skLineSegment(sketch, "E104.bottom", {"start": v(-35.57, 13.8) * mm, "end": v(-20.7, 13.8) * mm});
            skLineSegment(sketch, "E104.top", {"start": v(-35.57, -13.83) * mm, "end": v(-20.7, -13.83) * mm});
            skLineSegment(sketch, "E104.left", {"start": v(-35.57, 13.8) * mm, "end": v(-35.57, -13.83) * mm});
            skLineSegment(sketch, "E104.right", {"start": v(-20.7, 13.8) * mm, "end": v(-20.7, -13.83) * mm});
            skLineSegment(sketch, "E105.bottom", {"start": v(-86.96, 47.74) * mm, "end": v(14.52, 47.74) * mm});
            skLineSegment(sketch, "E105.top", {"start": v(-86.96, -45.67) * mm, "end": v(14.52, -45.67) * mm});
            skLineSegment(sketch, "E105.left", {"start": v(-86.96, 47.74) * mm, "end": v(-86.96, -45.67) * mm});
            skLineSegment(sketch, "E105.right", {"start": v(14.52, 47.74) * mm, "end": v(14.52, -45.67) * mm});
            skSolve(sketch);
        }
        {
            var Q0;
            Q0 = qSketchRegion(id + "F52", true);
            extrude(context, id + "F53", {"entities" : qUnion([Q0]), "operationType" : NewBodyOperationType.REMOVE, "oppositeDirection" : true, "depth" : 19 * mm});
        }
        {
            var Q0;
            Q0=makeQuery(id+"F53.boolean.opBoolean","COPY",EDGE,{"derivedFrom":makeQuery(id+"F53.opExtrude","CAP_EDGE",EDGE,{"disambiguationData":[OSD([sQuery(id+"F52.wireOp",EDGE,"E104.bottom")])],"isStart":false})});
            var Q1;
            Q1=makeQuery(id+"F53.boolean.opBoolean","COPY",EDGE,{"derivedFrom":makeQuery(id+"F53.opExtrude","CAP_EDGE",EDGE,{"disambiguationData":[OSD([sQuery(id+"F52.wireOp",EDGE,"E104.left")])],"isStart":false})});
            var Q2;
            Q2=makeQuery(id+"F53.boolean.opBoolean","COPY",EDGE,{"derivedFrom":makeQuery(id+"F53.opExtrude","CAP_EDGE",EDGE,{"disambiguationData":[OSD([sQuery(id+"F52.wireOp",EDGE,"E104.top")])],"isStart":false})});
            var Q3;
            Q3=makeQuery(id+"F53.boolean.opBoolean","COPY",EDGE,{"derivedFrom":makeQuery(id+"F53.opExtrude","CAP_EDGE",EDGE,{"disambiguationData":[OSD([sQuery(id+"F52.wireOp",EDGE,"E104.top")])],"isStart":true})});
            var Q4;
            Q4=makeQuery(id+"F53.boolean.opBoolean","COPY",EDGE,{"derivedFrom":makeQuery(id+"F53.opExtrude","CAP_EDGE",EDGE,{"disambiguationData":[OSD([sQuery(id+"F52.wireOp",EDGE,"E104.left")])],"isStart":true})});
            var Q5;
            Q5=makeQuery(id+"F53.boolean.opBoolean","COPY",EDGE,{"derivedFrom":makeQuery(id+"F53.opExtrude","CAP_EDGE",EDGE,{"disambiguationData":[OSD([sQuery(id+"F52.wireOp",EDGE,"E104.bottom")])],"isStart":true})});
            fillet(context, id + "F54", {"entities" : qUnion([Q0, Q1, Q2, Q3, Q4, Q5]), "radius" : 5 * mm, "tangentPropagation" : true, "allowEdgeOverflow" : false});
        }
    });
